# Revit family: Seat_Cover_Dispenser-Recessed-Bobrick-TrimLineSeries-B-3013
name_source: partatom
category: Specialty Equipment
units: mm (PartAtom-declared; Revit-internal decimal feet)

## family parameters
Cut with Voids When Loaded = No
Host = Face
OmniClass Number = 23.40.20.21
OmniClass Title = Toilet and Bath Specialties
Part Type = Normal
Room Calculation Point = No
Round Connector Dimension = Use Diameter
Shared = Yes

## types (1)
- B-3013
    Assembly Code = C1030200
    Default Elevation = 42 15/32"
    Description = TrimLineSeries Recessed Seat-Cover Dispenser
    Finish = Stainless Steel-Bobrick-Type 304-Satin
    Height = 13 1/16"
    Installation Type = Recessed in Wall
    Length = 9/16"
    Manufacturer = Bobrick
    Material = Stainless Steel-Bobrick-Type 304-Satin
    Model = B-3013
    Price = Prices may vary. Please consult Manufacturer Representative for most up-to-date price list.
    Product Documentation Link = https://www.bobrick.com
    Product Page URL = https://www.bobrick.com
    Revised Date = 11/03/2020
    Specification = Recessed toilet-seat-cover dispenser shall be type-304 stainless steel with all-welded construction; exposed surfaces shall have satin finish. Door shall be 18 gauge (1.2mm); have 9/16" (14mm) 90° return edges; be secured to cabinet with a concealed, fulllength stainless steel piano-hinge; and equipped with a tumbler lock keyed like other Bobrick washroom accessories. Dispenser shall have a minimum capacity of 500 paper toilet seat covers. Manufacturer’s service and parts manual shall be provided to the building owner/manager upon request. Recessed Toilet-Seat-Cover Dispenser shall be Model B-3013 of Bobrick Washroom Equipment, Inc., Clifton Park, New York; Jackson, Tennessee; Los Angeles, California; Bobrick Washroom Equipment Company, Scarborough, Ontario; Bobrick Washroom Equipment Pty. Ltd., Australia; and Bobrick Washroom Equipment Limited, United Kingdom.
    URL = http://www.bobrick.com
    Warranty Information = 1 Year Limited Warranty
    Width = 17 9/16"

## geometry (parser evidence)
native form markers: Sweep x3
no freeform markers — native parametric forms only
